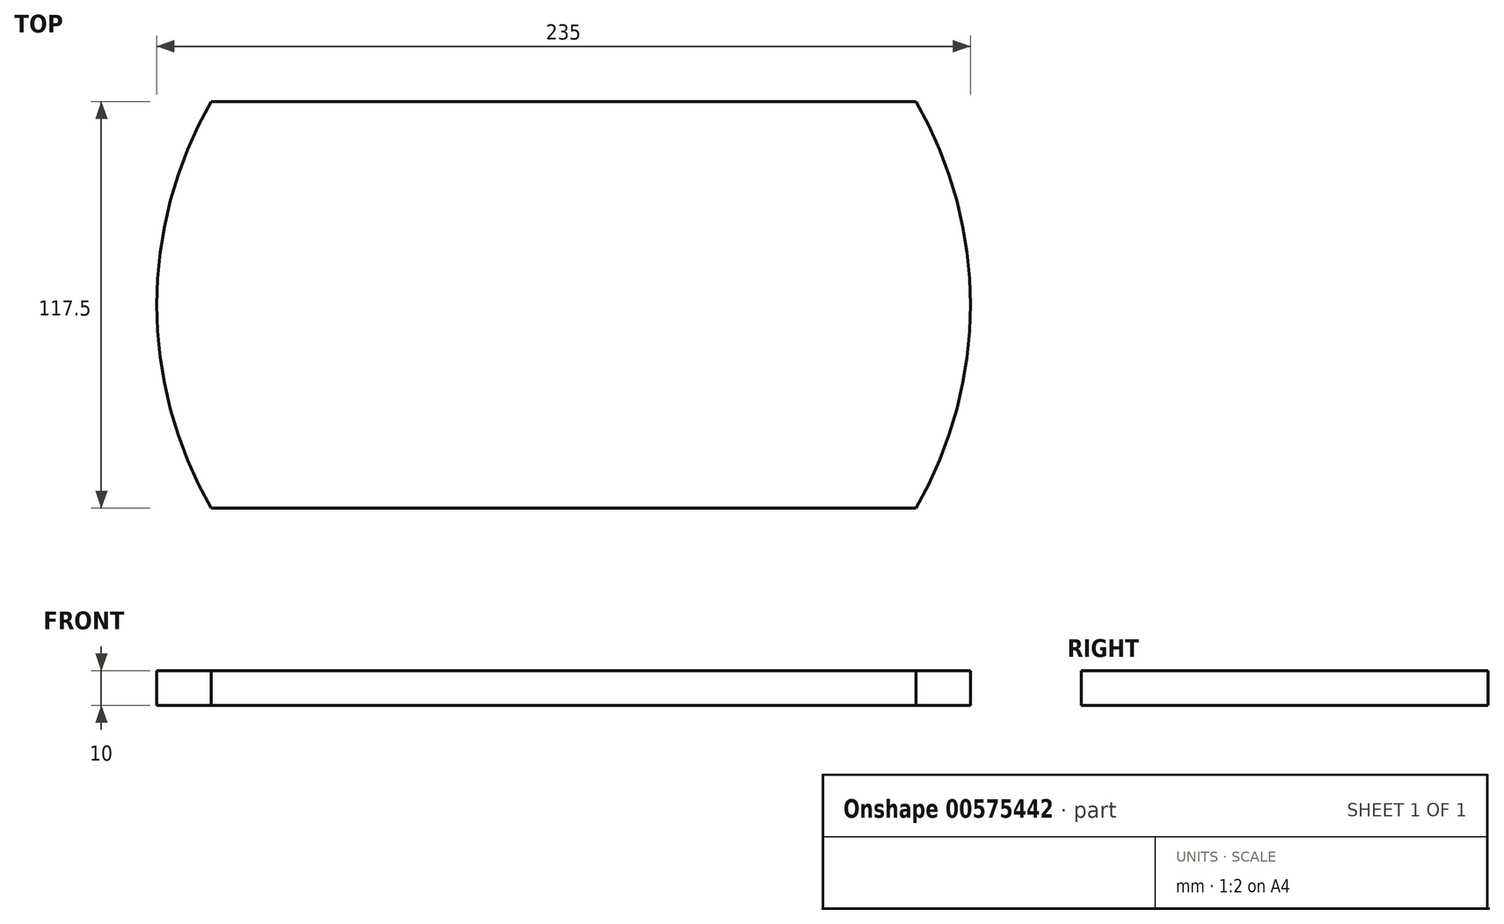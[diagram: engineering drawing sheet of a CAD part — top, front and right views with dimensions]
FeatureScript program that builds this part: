
annotation { "Feature Type Name" : "Feature", "Feature Type Description" : "" }
export const myFeature = defineFeature(function(context is Context, id is Id, definition is map)
    precondition{}
    {
        {
            var Q0;
            Q0=qCreatedBy(makeId("Top.planeOp"),FACE);
            var sketch = newSketch(context, id + "F0", { "sketchPlane" : qUnion([Q0])});
            skArc(sketch, "E0", {"start": v(-101.76, 58.75) * mm, "mid": v(-117.5, 0) * mm, "end": v(-101.76, -58.75) * mm});
            skLineSegment(sketch, "E1", {"start": v(0, 58.75) * mm, "end": v(-101.76, 58.75) * mm});
            skLineSegment(sketch, "E2", {"start": v(-101.76, 58.75) * mm, "end": v(101.76, 58.75) * mm});
            skLineSegment(sketch, "E3", {"start": v(0, -58.75) * mm, "end": v(-101.76, -58.75) * mm});
            skLineSegment(sketch, "E4", {"start": v(-101.76, -58.75) * mm, "end": v(101.76, -58.75) * mm});
            skArc(sketch, "E5.trimOffspring", {"start": v(101.76, -58.75) * mm, "mid": v(117.5, 0) * mm, "end": v(101.76, 58.75) * mm});
            skSolve(sketch);
        }
        {
            var Q0;
            {var subQ0=sQuery(id+"F0.wireOp",EDGE,"E0");Q0=makeQuery(id+"F0.imprint","IMPRINT",FACE,{"disambiguationData":[TD([[makeQuery(id+"F0.imprint","IMPRINT",EDGE,{"derivedFrom":subQ0}),1.0]])]});}
            extrude(context, id + "F1", {"entities" : qUnion([Q0]), "depth" : 10 * mm, "offsetDistance" : 25 * mm});
        }
    });
